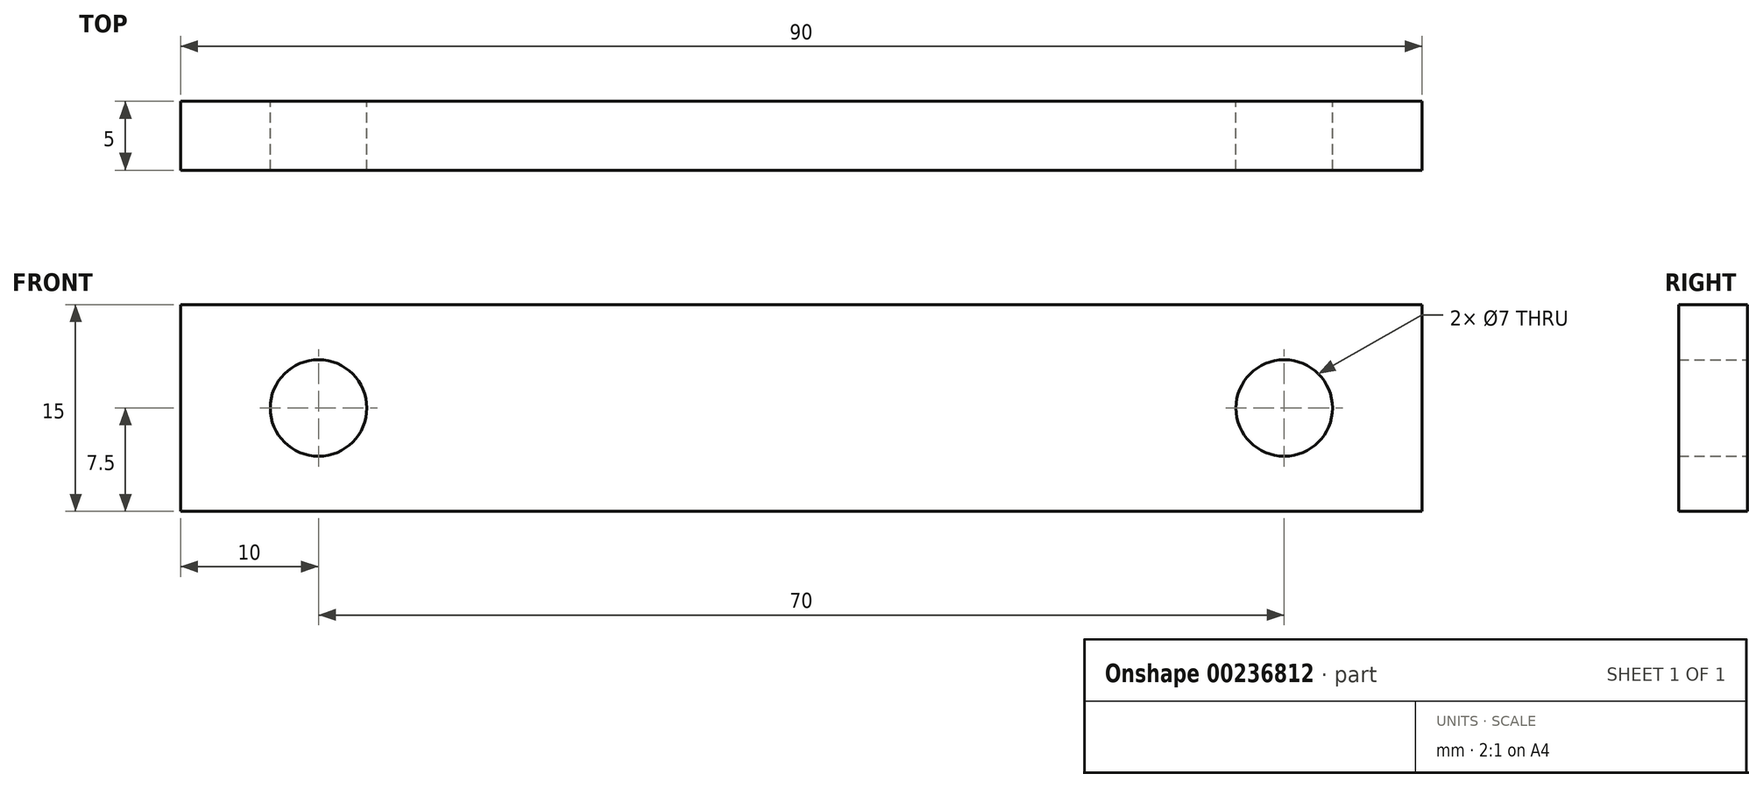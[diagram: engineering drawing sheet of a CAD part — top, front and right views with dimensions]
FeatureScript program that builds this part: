
annotation { "Feature Type Name" : "Feature", "Feature Type Description" : "" }
export const myFeature = defineFeature(function(context is Context, id is Id, definition is map)
    precondition{}
    {
        {
            var Q0;
            Q0=qCreatedBy(makeId("Front.planeOp"),FACE);
            var sketch = newSketch(context, id + "F0", { "sketchPlane" : qUnion([Q0])});
            skLineSegment(sketch, "E0.bottom", {"start": v(45, -7.5) * mm, "end": v(-45, -7.5) * mm});
            skLineSegment(sketch, "E0.top", {"start": v(45, 7.5) * mm, "end": v(-45, 7.5) * mm});
            skLineSegment(sketch, "E0.left", {"start": v(45, -7.5) * mm, "end": v(45, 7.5) * mm});
            skLineSegment(sketch, "E0.right", {"start": v(-45, -7.5) * mm, "end": v(-45, 7.5) * mm});
            skPoint(sketch, "E0.middle", {"position": v(0, 0) * mm});
            skCircle(sketch, "E1", {"center": v(-35, 0) * mm, "radius": 3.5 * mm});
            skPoint(sketch, "E1.centerSnap0", {"position": v(-45, 0) * mm});
            skCircle(sketch, "E2", {"center": v(35, 0) * mm, "radius": 3.5 * mm});
            skPoint(sketch, "E2.centerSnap0", {"position": v(45, 0) * mm});
            skSolve(sketch);
        }
        {
            var Q0;
            Q0=makeQuery(id+"F0.imprint","IMPRINT",FACE,{"disambiguationData":[TD([[makeQuery(id+"F0.imprint","IMPRINT",EDGE,{"derivedFrom":sQuery(id+"F0.wireOp",EDGE,"E0.bottom")}),-1.0]])]});
            extrude(context, id + "F1", {"entities" : qUnion([Q0]), "depth" : 5 * mm});
        }
    });
